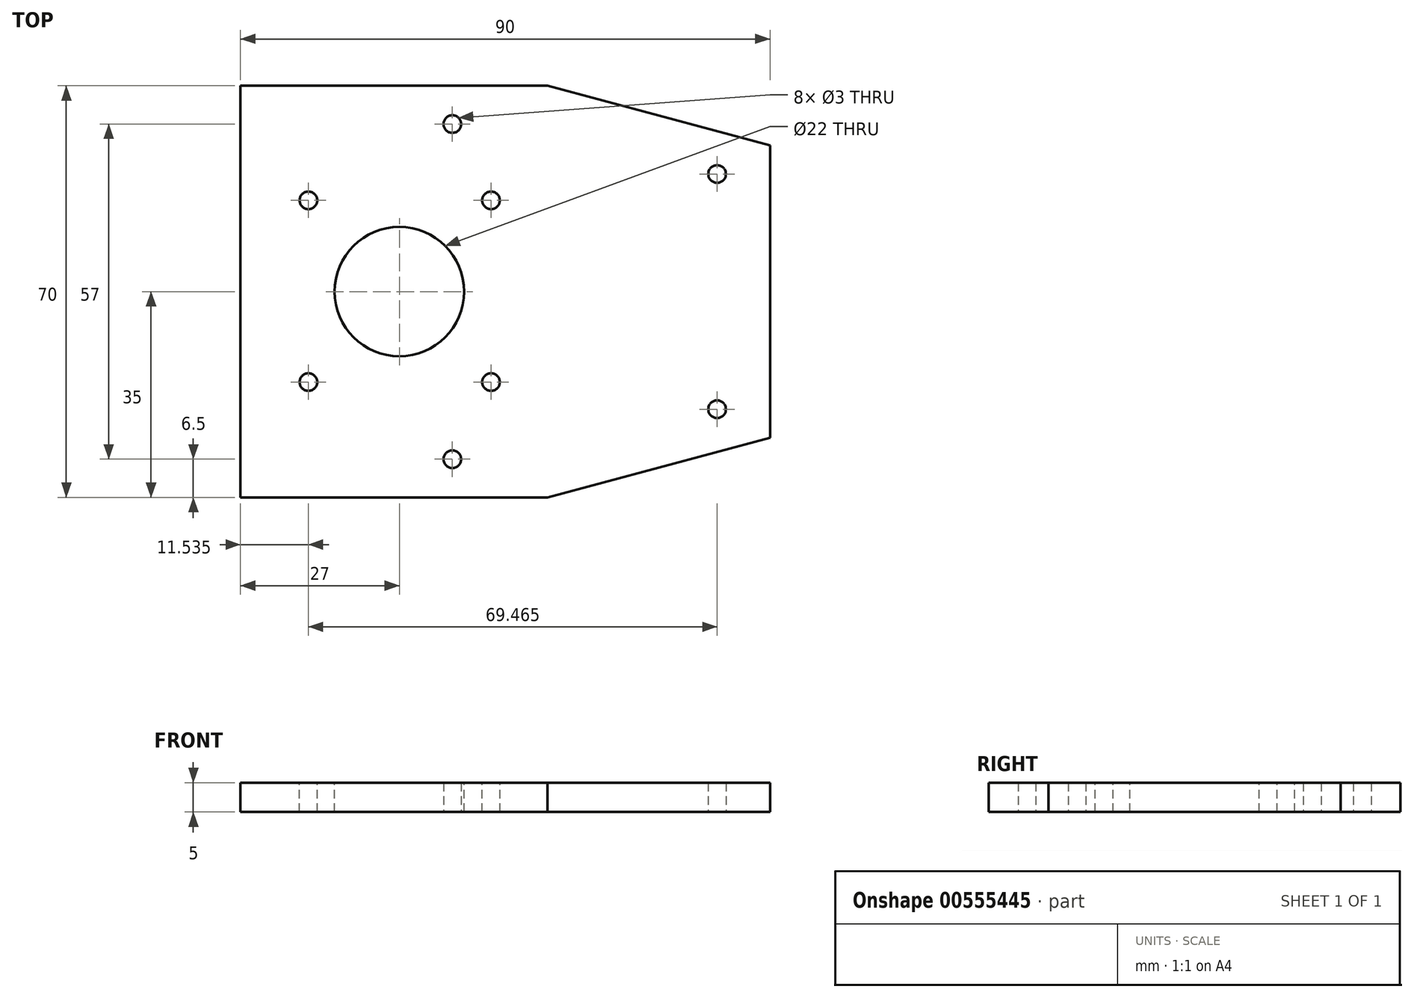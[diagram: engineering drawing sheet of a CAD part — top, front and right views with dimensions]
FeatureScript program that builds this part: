
annotation { "Feature Type Name" : "Feature", "Feature Type Description" : "" }
export const myFeature = defineFeature(function(context is Context, id is Id, definition is map)
    precondition{}
    {
        {
            var Q0;
            Q0=qCreatedBy(makeId("Top.planeOp"),FACE);
            var sketch = newSketch(context, id + "F0", { "sketchPlane" : qUnion([Q0])});
            skLineSegment(sketch, "E0.bottom", {"start": v(45, 35) * mm, "end": v(-45, 35) * mm});
            skLineSegment(sketch, "E0.top", {"start": v(45, -35) * mm, "end": v(-45, -35) * mm});
            skLineSegment(sketch, "E0.left", {"start": v(45, 35) * mm, "end": v(45, -35) * mm});
            skLineSegment(sketch, "E0.right", {"start": v(-45, 35) * mm, "end": v(-45, -35) * mm});
            skPoint(sketch, "E0.middle", {"position": v(0, 0) * mm});
            skLineSegment(sketch, "E1", {"start": v(-62.53, 0) * mm, "end": v(57.54, 0) * mm, "construction": true});
            skPoint(sketch, "E1.endSnap0", {"position": v(45, 0) * mm});
            skLineSegment(sketch, "E2", {"start": v(-9, 28.5) * mm, "end": v(56.7, 28.5) * mm, "construction": true});
            skLineSegment(sketch, "E3", {"start": v(36, 42.86) * mm, "end": v(36, -39.95) * mm, "construction": true});
            skLineSegment(sketch, "E4", {"start": v(-37.3, 43.03) * mm, "end": v(-37.3, -39.95) * mm, "construction": true});
            skLineSegment(sketch, "E5", {"start": v(-9, 42.86) * mm, "end": v(-9, -39.61) * mm, "construction": true});
            skLineSegment(sketch, "E6.trimOffspring", {"start": v(36, 20) * mm, "end": v(57.37, 20) * mm, "construction": true});
            skLineSegment(sketch, "E7", {"start": v(-9, -28.5) * mm, "end": v(55.89, -28.5) * mm, "construction": true});
            skLineSegment(sketch, "E8", {"start": v(36, -20) * mm, "end": v(57.75, -20) * mm, "construction": true});
            skCircle(sketch, "E9", {"center": v(36, 20) * mm, "radius": 1.5 * mm});
            skCircle(sketch, "E10", {"center": v(36, -20) * mm, "radius": 1.5 * mm});
            skCircle(sketch, "E11", {"center": v(-9, 28.5) * mm, "radius": 1.5 * mm});
            skCircle(sketch, "E12", {"center": v(-9, -28.5) * mm, "radius": 1.5 * mm});
            skSolve(sketch);
        }
        {
            var Q0;
            Q0=makeQuery(id+"F0.imprint","IMPRINT",FACE,{"disambiguationData":[TD([[makeQuery(id+"F0.imprint","IMPRINT",EDGE,{"derivedFrom":sQuery(id+"F0.wireOp",EDGE,"E0.bottom")}),1.0]])]});
            var sketch = newSketch(context, id + "F1", { "sketchPlane" : qUnion([Q0])});
            skLineSegment(sketch, "E13", {"start": v(0, -15.5) * mm, "end": v(-38.24, -15.5) * mm, "construction": true});
            skLineSegment(sketch, "E14", {"start": v(0, 15.5) * mm, "end": v(-37.32, 15.5) * mm, "construction": true});
            skLineSegment(sketch, "E15", {"start": v(-18, 42.06) * mm, "end": v(-18, -39.22) * mm, "construction": true});
            skCircle(sketch, "E16", {"center": v(-18, 0) * mm, "radius": 56112.5 * mm});
            skLineSegment(sketch, "E17", {"start": v(-33.5, 29.7) * mm, "end": v(-33.5, -28.39) * mm, "construction": true});
            skLineSegment(sketch, "E18", {"start": v(-2.5, 25.47) * mm, "end": v(-2.5, -26.35) * mm, "construction": true});
            skCircle(sketch, "E19", {"center": v(-33.5, 15.5) * mm, "radius": 1.5 * mm});
            skCircle(sketch, "E20", {"center": v(-2.5, 15.5) * mm, "radius": 1.5 * mm});
            skCircle(sketch, "E21", {"center": v(-33.5, -15.5) * mm, "radius": 1.5 * mm});
            skCircle(sketch, "E22", {"center": v(-2.5, -15.5) * mm, "radius": 1.5 * mm});
            skCircle(sketch, "E23", {"center": v(-18, 0) * mm, "radius": 11 * mm});
            skSolve(sketch);
        }
        {
            var Q0;
            Q0=makeQuery(id+"F0.imprint","IMPRINT",FACE,{"disambiguationData":[TD([[makeQuery(id+"F0.imprint","IMPRINT",EDGE,{"derivedFrom":sQuery(id+"F0.wireOp",EDGE,"E0.bottom")}),1.0]])]});
            extrude(context, id + "F2", {"entities" : qUnion([Q0]), "depth" : 5 * mm, "offsetDistance" : 25 * mm});
        }
        {
            var Q0;
            Q0=makeQuery(id+"F2.opExtrude","CAP_FACE",FACE,{"disambiguationData":[OSD([sQuery(id+"F0.wireOp",EDGE,"E0.bottom"),sQuery(id+"F0.wireOp",EDGE,"E0.top"),sQuery(id+"F0.wireOp",EDGE,"E0.left"),sQuery(id+"F0.wireOp",EDGE,"E0.right"),sQuery(id+"F0.wireOp",EDGE,"E9"),sQuery(id+"F0.wireOp",EDGE,"E10"),sQuery(id+"F0.wireOp",EDGE,"E11"),sQuery(id+"F0.wireOp",EDGE,"E12")])],"isStart":false});
            var sketch = newSketch(context, id + "F3", { "sketchPlane" : qUnion([Q0])});
            skPoint(sketch, "E24", {"position": v(-17.94, 0) * mm});
            skPoint(sketch, "E25", {"position": v(-2.42, 15.52) * mm});
            skPoint(sketch, "E26", {"position": v(-33.47, 15.52) * mm});
            skPoint(sketch, "E27", {"position": v(-2.42, -15.38) * mm});
            skPoint(sketch, "E28", {"position": v(-33.47, -15.38) * mm});
            skSolve(sketch);
        }
        {
            var Q0;
            Q0=sQuery(id+"F3.wireOp",VERTEX,"E25");
            var Q1;
            Q1=sQuery(id+"F3.wireOp",VERTEX,"E27");
            var Q2;
            Q2=sQuery(id+"F3.wireOp",VERTEX,"E28");
            var Q3;
            Q3=sQuery(id+"F3.wireOp",VERTEX,"E26");
            var Q4;
            Q4=makeQuery(id+"F2.opExtrude","SWEPT_BODY",BODY,{"disambiguationData":[OSD([sQuery(id+"F0.wireOp",EDGE,"E0.bottom"),sQuery(id+"F0.wireOp",EDGE,"E0.top"),sQuery(id+"F0.wireOp",EDGE,"E0.left"),sQuery(id+"F0.wireOp",EDGE,"E0.right"),sQuery(id+"F0.wireOp",EDGE,"E9"),sQuery(id+"F0.wireOp",EDGE,"E10"),sQuery(id+"F0.wireOp",EDGE,"E11"),sQuery(id+"F0.wireOp",EDGE,"E12")])]});
            hole(context, id + "F4", {"style" : HoleStyle.SIMPLE, "endStyle" : HoleEndStyle.THROUGH, "holeDiameter" : 3 * mm, "isTappedThrough" : true, "tappedDepth" : 12 * mm, "tapClearance" : 3, "locations" : qUnion([Q0, Q1, Q2, Q3]), "scope" : qUnion([Q4])});
        }
        {
            var Q0;
            Q0=sQuery(id+"F1.wireOp",VERTEX,"E16.center");
            var Q1;
            Q1=makeQuery(id+"F2.opExtrude","SWEPT_BODY",BODY,{"disambiguationData":[OSD([sQuery(id+"F0.wireOp",EDGE,"E0.bottom"),sQuery(id+"F0.wireOp",EDGE,"E0.top"),sQuery(id+"F0.wireOp",EDGE,"E0.left"),sQuery(id+"F0.wireOp",EDGE,"E0.right"),sQuery(id+"F0.wireOp",EDGE,"E9"),sQuery(id+"F0.wireOp",EDGE,"E10"),sQuery(id+"F0.wireOp",EDGE,"E11"),sQuery(id+"F0.wireOp",EDGE,"E12")])]});
            hole(context, id + "F5", {"style" : HoleStyle.SIMPLE, "endStyle" : HoleEndStyle.THROUGH, "oppositeDirection" : true, "holeDiameter" : 11.5 * mm, "isTappedThrough" : true, "tappedDepth" : 12 * mm, "tapClearance" : 3, "locations" : qUnion([Q0]), "scope" : qUnion([Q1])});
        }
        {
            var Q0;
            Q0=makeQuery(id+"F2.opExtrude","CAP_FACE",FACE,{"disambiguationData":[OSD([sQuery(id+"F0.wireOp",EDGE,"E0.bottom"),sQuery(id+"F0.wireOp",EDGE,"E0.top"),sQuery(id+"F0.wireOp",EDGE,"E0.left"),sQuery(id+"F0.wireOp",EDGE,"E0.right"),sQuery(id+"F0.wireOp",EDGE,"E9"),sQuery(id+"F0.wireOp",EDGE,"E10"),sQuery(id+"F0.wireOp",EDGE,"E11"),sQuery(id+"F0.wireOp",EDGE,"E12")])],"isStart":false});
            var sketch = newSketch(context, id + "F6", { "sketchPlane" : qUnion([Q0])});
            skPoint(sketch, "E29", {"position": v(7.16, 35) * mm});
            skPoint(sketch, "E30", {"position": v(45, 24.84) * mm});
            skPoint(sketch, "E31", {"position": v(45, -24.94) * mm});
            skPoint(sketch, "E32", {"position": v(7.16, -35) * mm});
            skLineSegment(sketch, "E33", {"start": v(45, 24.84) * mm, "end": v(7.16, 35) * mm});
            skLineSegment(sketch, "E34", {"start": v(45, -24.94) * mm, "end": v(7.16, -35) * mm});
            skSolve(sketch);
        }
        {
            var Q0;
            {var subQ0=sQuery(id+"F6.wireOp",EDGE,"E33");Q0=makeQuery(id+"F6.imprint","IMPRINT",FACE,{"disambiguationData":[TD([[makeQuery(id+"F6.imprint","IMPRINT",EDGE,{"derivedFrom":subQ0}),-1.0]])]});}
            extrude(context, id + "F7", {"entities" : qUnion([Q0]), "operationType" : NewBodyOperationType.REMOVE, "oppositeDirection" : true, "depth" : 5 * mm, "offsetDistance" : 25 * mm});
        }
        {
            var Q0;
            Q0=makeQuery(id+"F2.opExtrude","CAP_FACE",FACE,{"disambiguationData":[OSD([sQuery(id+"F0.wireOp",EDGE,"E0.bottom"),sQuery(id+"F0.wireOp",EDGE,"E0.top"),sQuery(id+"F0.wireOp",EDGE,"E0.left"),sQuery(id+"F0.wireOp",EDGE,"E0.right"),sQuery(id+"F0.wireOp",EDGE,"E9"),sQuery(id+"F0.wireOp",EDGE,"E10"),sQuery(id+"F0.wireOp",EDGE,"E11"),sQuery(id+"F0.wireOp",EDGE,"E12")])],"isStart":false});
            var sketch = newSketch(context, id + "F8", { "sketchPlane" : qUnion([Q0])});
            skLineSegment(sketch, "E35", {"start": v(7.02, -35) * mm, "end": v(45, -25.13) * mm});
            skSolve(sketch);
        }
        {
            var Q0;
            {var subQ0=sQuery(id+"F8.wireOp",EDGE,"E35");Q0=makeQuery(id+"F8.imprint","IMPRINT",FACE,{"disambiguationData":[TD([[makeQuery(id+"F8.imprint","IMPRINT",EDGE,{"derivedFrom":subQ0}),-1.0]])]});}
            extrude(context, id + "F9", {"entities" : qUnion([Q0]), "operationType" : NewBodyOperationType.REMOVE, "depth" : 0.1 * mm, "offsetDistance" : 25 * mm});
        }
        {
            var Q0;
            Q0=makeQuery(id+"F2.opExtrude","CAP_FACE",FACE,{"disambiguationData":[OSD([sQuery(id+"F0.wireOp",EDGE,"E0.bottom"),sQuery(id+"F0.wireOp",EDGE,"E0.top"),sQuery(id+"F0.wireOp",EDGE,"E0.left"),sQuery(id+"F0.wireOp",EDGE,"E0.right"),sQuery(id+"F0.wireOp",EDGE,"E9"),sQuery(id+"F0.wireOp",EDGE,"E10"),sQuery(id+"F0.wireOp",EDGE,"E11"),sQuery(id+"F0.wireOp",EDGE,"E12")])],"isStart":false});
            var sketch = newSketch(context, id + "F10", { "sketchPlane" : qUnion([Q0])});
            skCircle(sketch, "E36", {"center": v(-18, 0) * mm, "radius": 11 * mm});
            skSolve(sketch);
        }
        {
            var Q0;
            Q0=makeQuery(id+"F10.imprint","IMPRINT",FACE,{"disambiguationData":[TD([[makeQuery(id+"F10.imprint","IMPRINT",EDGE,{"derivedFrom":sQuery(id+"F10.wireOp",EDGE,"E36")}),1.0]])]});
            extrude(context, id + "F11", {"entities" : qUnion([Q0]), "operationType" : NewBodyOperationType.REMOVE, "endBound" : BoundingType.THROUGH_ALL, "oppositeDirection" : true, "depth" : 25 * mm, "offsetDistance" : 25 * mm});
        }
        {
            var Q0;
            Q0=makeQuery(id+"F2.opExtrude","CAP_FACE",FACE,{"disambiguationData":[OSD([sQuery(id+"F0.wireOp",EDGE,"E0.bottom"),sQuery(id+"F0.wireOp",EDGE,"E0.top"),sQuery(id+"F0.wireOp",EDGE,"E0.left"),sQuery(id+"F0.wireOp",EDGE,"E0.right"),sQuery(id+"F0.wireOp",EDGE,"E9"),sQuery(id+"F0.wireOp",EDGE,"E10"),sQuery(id+"F0.wireOp",EDGE,"E11"),sQuery(id+"F0.wireOp",EDGE,"E12")])],"isStart":false});
            var sketch = newSketch(context, id + "F12", { "sketchPlane" : qUnion([Q0])});
            skLineSegment(sketch, "E37", {"start": v(58.3, 0) * mm, "end": v(-57.87, 0) * mm, "construction": true});
            skLineSegment(sketch, "E38", {"start": v(45, 24.84) * mm, "end": v(60.16, 24.84) * mm, "construction": true});
            skLineSegment(sketch, "E39", {"start": v(7.16, 35) * mm, "end": v(7.16, -41.55) * mm, "construction": true});
            skLineSegment(sketch, "E40", {"start": v(54.23, -24.84) * mm, "end": v(-50.08, -24.84) * mm, "construction": true});
            skLineSegment(sketch, "E41", {"start": v(7.16, -35) * mm, "end": v(45, -24.84) * mm});
            skSolve(sketch);
        }
        {
            var Q0;
            {var subQ0=sQuery(id+"F12.wireOp",EDGE,"E41");Q0=makeQuery(id+"F12.imprint","IMPRINT",FACE,{"disambiguationData":[TD([[makeQuery(id+"F12.imprint","IMPRINT",EDGE,{"derivedFrom":subQ0}),-1.0]])]});}
            extrude(context, id + "F13", {"entities" : qUnion([Q0]), "operationType" : NewBodyOperationType.REMOVE, "endBound" : BoundingType.THROUGH_ALL, "oppositeDirection" : true, "depth" : 25 * mm, "offsetDistance" : 25 * mm});
        }
    });
